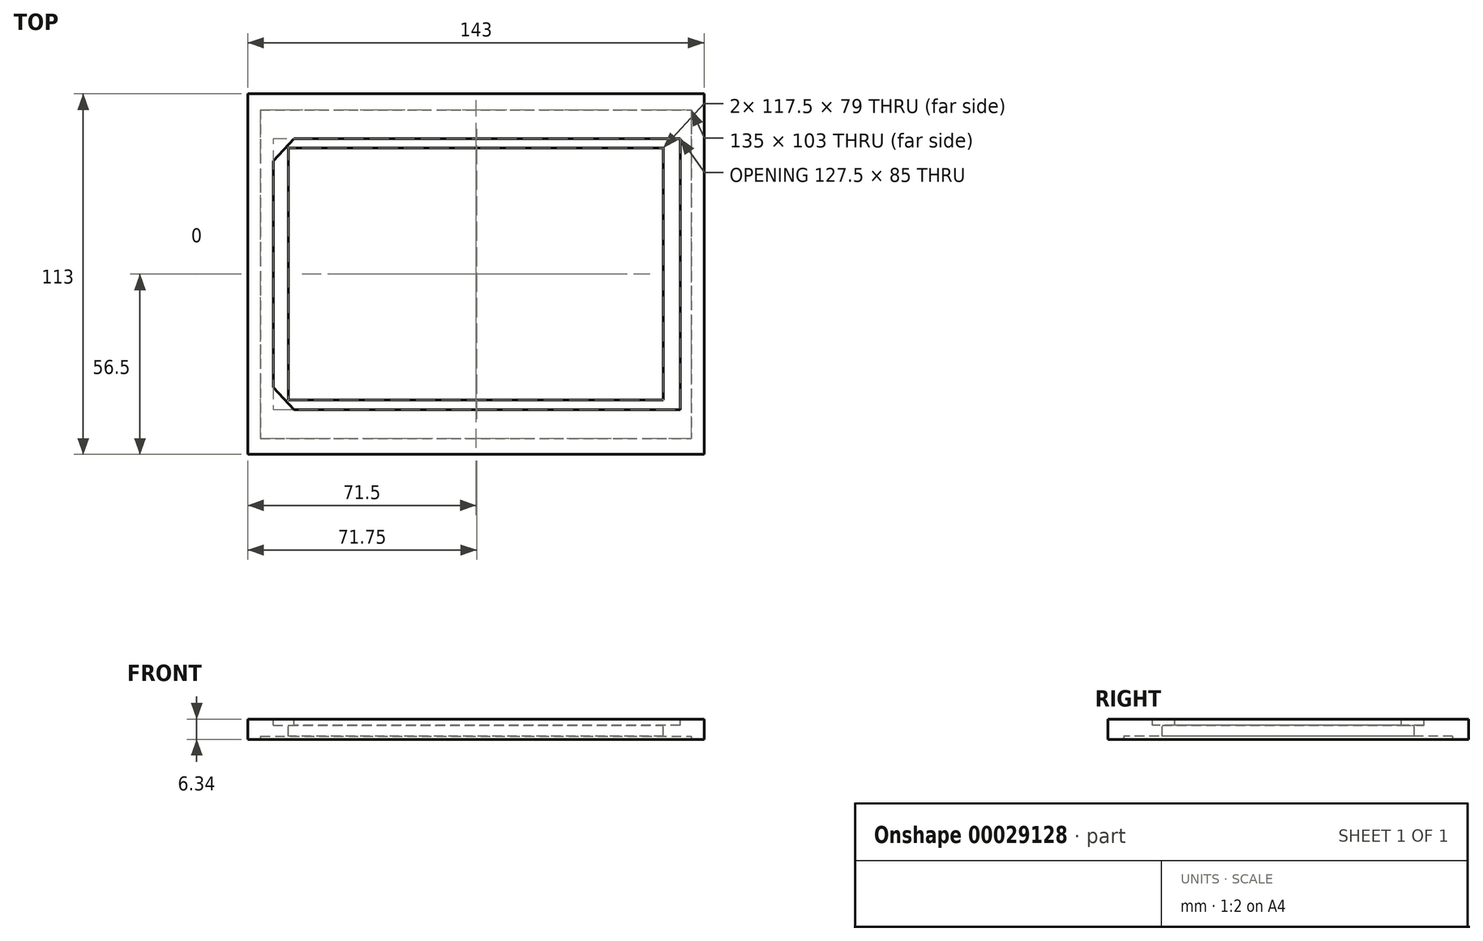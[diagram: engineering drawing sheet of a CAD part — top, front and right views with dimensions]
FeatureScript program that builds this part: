
annotation { "Feature Type Name" : "Feature", "Feature Type Description" : "" }
export const myFeature = defineFeature(function(context is Context, id is Id, definition is map)
    precondition{}
    {
        {
            var Q0;
            Q0=qCreatedBy(makeId("Top.planeOp"),FACE);
            var sketch = newSketch(context, id + "F0", { "sketchPlane" : qUnion([Q0])});
            skLineSegment(sketch, "E0.rect.bottom", {"start": v(71.5, -56.5) * mm, "end": v(-71.5, -56.5) * mm});
            skLineSegment(sketch, "E0.rect.top", {"start": v(71.5, 56.5) * mm, "end": v(-71.5, 56.5) * mm});
            skLineSegment(sketch, "E0.rect.left", {"start": v(71.5, -56.5) * mm, "end": v(71.5, 56.5) * mm});
            skLineSegment(sketch, "E0.rect.right", {"start": v(-71.5, -56.5) * mm, "end": v(-71.5, 56.5) * mm});
            skPoint(sketch, "E0.rect.middle", {"position": v(0, 0) * mm});
            skSolve(sketch);
        }
        {
            var Q0;
            Q0=makeQuery(id+"F0.imprint","IMPRINT",FACE,{"disambiguationData":[TD([[makeQuery(id+"F0.imprint","IMPRINT",EDGE,{"derivedFrom":sQuery(id+"F0.wireOp",EDGE,"E0.rect.bottom")}),-1.0]])]});
            extrude(context, id + "F1", {"entities" : qUnion([Q0]), "endBound" : BoundingType.SYMMETRIC, "depth" : 6.35 * mm});
        }
        {
            var Q0;
            Q0=makeQuery(id+"F1.opExtrude","CAP_FACE",FACE,{"disambiguationData":[OSD([sQuery(id+"F0.wireOp",EDGE,"E0.rect.bottom"),sQuery(id+"F0.wireOp",EDGE,"E0.rect.top"),sQuery(id+"F0.wireOp",EDGE,"E0.rect.left"),sQuery(id+"F0.wireOp",EDGE,"E0.rect.right")])],"isStart":false});
            var sketch = newSketch(context, id + "F2", { "sketchPlane" : qUnion([Q0])});
            skPoint(sketch, "E1.rect.middle", {"position": v(0, 0) * mm});
            skLineSegment(sketch, "E2.rect.bottom", {"start": v(64, 42.5) * mm, "end": v(-57, 42.5) * mm});
            skLineSegment(sketch, "E2.rect.top", {"start": v(64, -42.5) * mm, "end": v(-57, -42.5) * mm});
            skLineSegment(sketch, "E2.rect.left", {"start": v(64, 42.5) * mm, "end": v(64, -42.5) * mm});
            skLineSegment(sketch, "E2.rect.right", {"start": v(-63.5, 35.5) * mm, "end": v(-63.5, -35.5) * mm});
            skLineSegment(sketch, "E3", {"start": v(-63.5, 35.5) * mm, "end": v(-57, 42.5) * mm});
            skLineSegment(sketch, "E4", {"start": v(-63.5, -35.5) * mm, "end": v(-57, -42.5) * mm});
            skSolve(sketch);
        }
        {
            var Q0;
            Q0=makeQuery(id+"F1.opExtrude","CAP_FACE",FACE,{"disambiguationData":[OSD([sQuery(id+"F0.wireOp",EDGE,"E0.rect.bottom"),sQuery(id+"F0.wireOp",EDGE,"E0.rect.top"),sQuery(id+"F0.wireOp",EDGE,"E0.rect.left"),sQuery(id+"F0.wireOp",EDGE,"E0.rect.right")])],"isStart":false});
            var sketch = newSketch(context, id + "F3", { "sketchPlane" : qUnion([Q0])});
            skLineSegment(sketch, "E5.rect.bottom", {"start": v(58.75, 39.5) * mm, "end": v(-58.75, 39.5) * mm});
            skLineSegment(sketch, "E5.rect.top", {"start": v(58.75, -39.5) * mm, "end": v(-58.75, -39.5) * mm});
            skLineSegment(sketch, "E5.rect.left", {"start": v(58.75, 39.5) * mm, "end": v(58.75, -39.5) * mm});
            skLineSegment(sketch, "E5.rect.right", {"start": v(-58.75, 39.5) * mm, "end": v(-58.75, -39.5) * mm});
            skPoint(sketch, "E5.rect.middle", {"position": v(0, 0) * mm});
            skSolve(sketch);
        }
        {
            var Q0;
            Q0=makeQuery(id+"F3.imprint","IMPRINT",FACE,{"disambiguationData":[TD([[makeQuery(id+"F3.imprint","IMPRINT",EDGE,{"derivedFrom":sQuery(id+"F3.wireOp",EDGE,"E5.rect.bottom")}),1.0]])]});
            extrude(context, id + "F4", {"entities" : qUnion([Q0]), "operationType" : NewBodyOperationType.REMOVE, "oppositeDirection" : true, "depth" : 25.4 * mm});
        }
        {
            var Q0;
            Q0=qSketchRegion(id+"F2",true);
            extrude(context, id + "F5", {"entities" : qUnion([Q0]), "operationType" : NewBodyOperationType.REMOVE, "oppositeDirection" : true, "depth" : 2 * mm});
        }
        {
            var Q0;
            Q0=makeQuery(id+"F1.opExtrude","CAP_FACE",FACE,{"disambiguationData":[OSD([sQuery(id+"F0.wireOp",EDGE,"E0.rect.bottom"),sQuery(id+"F0.wireOp",EDGE,"E0.rect.top"),sQuery(id+"F0.wireOp",EDGE,"E0.rect.left"),sQuery(id+"F0.wireOp",EDGE,"E0.rect.right")])],"isStart":true});
            var sketch = newSketch(context, id + "F6", { "sketchPlane" : qUnion([Q0])});
            skLineSegment(sketch, "E6.rect.bottom", {"start": v(-67.5, -51.5) * mm, "end": v(67.5, -51.5) * mm});
            skLineSegment(sketch, "E6.rect.top", {"start": v(-67.5, 51.5) * mm, "end": v(67.5, 51.5) * mm});
            skLineSegment(sketch, "E6.rect.left", {"start": v(-67.5, -51.5) * mm, "end": v(-67.5, 51.5) * mm});
            skLineSegment(sketch, "E6.rect.right", {"start": v(67.5, -51.5) * mm, "end": v(67.5, 51.5) * mm});
            skPoint(sketch, "E6.rect.middle", {"position": v(0, 0) * mm});
            skSolve(sketch);
        }
        {
            var Q0;
            Q0=qSketchRegion(id+"F6",true);
            extrude(context, id + "F7", {"entities" : qUnion([Q0]), "operationType" : NewBodyOperationType.REMOVE, "oppositeDirection" : true, "depth" : 1 * mm});
        }
    });
